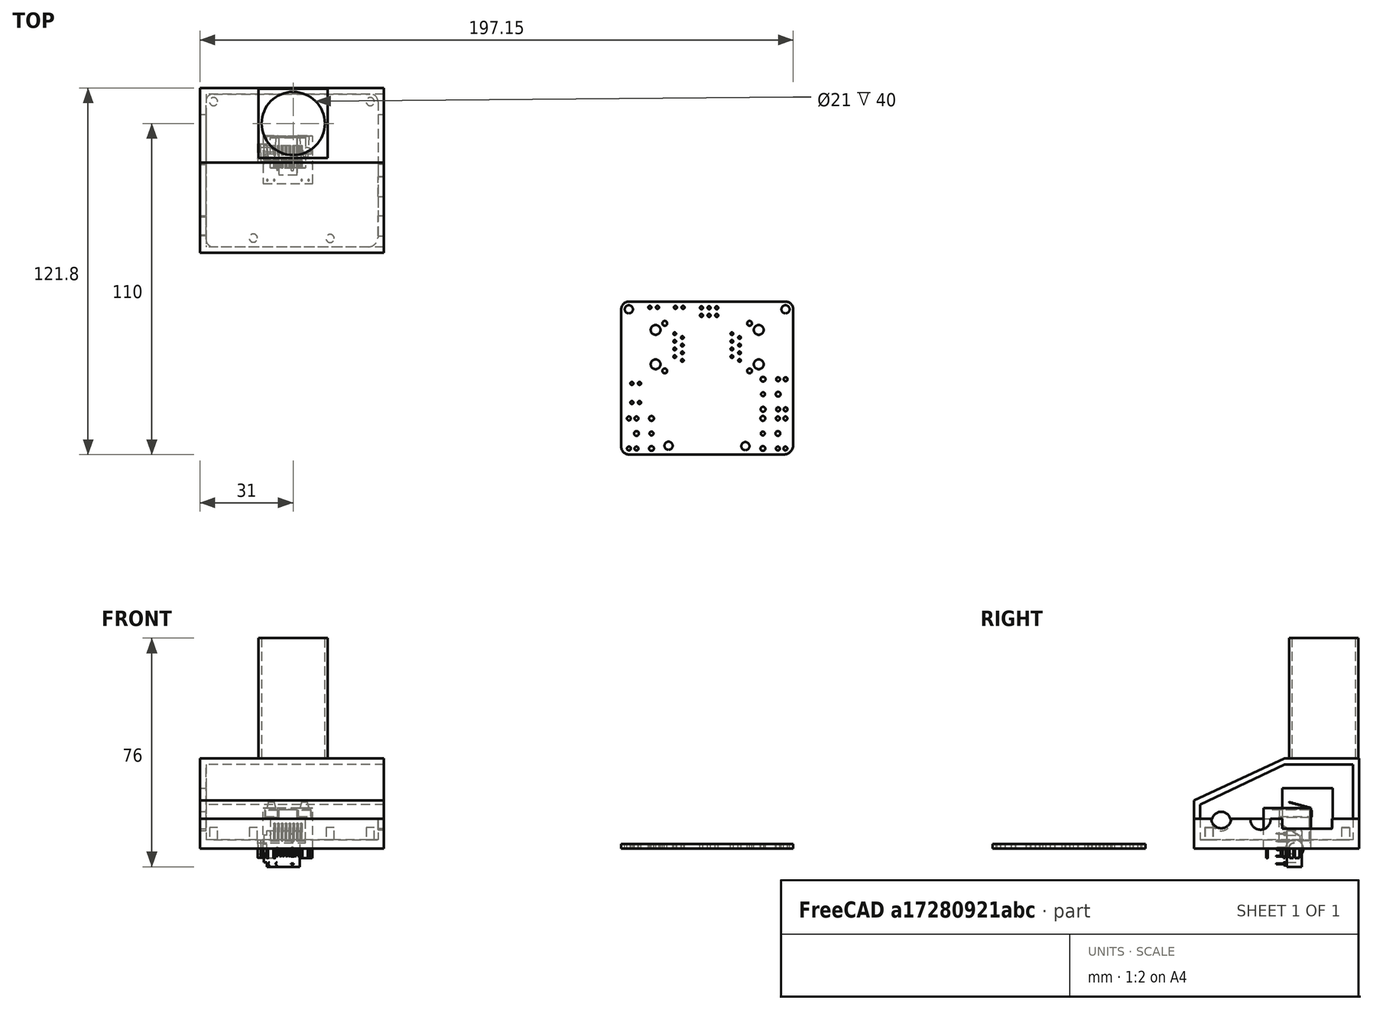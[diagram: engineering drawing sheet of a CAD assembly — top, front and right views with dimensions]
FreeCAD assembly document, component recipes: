
FREECAD ASSEMBLY — COMPONENT RECIPES ("FT81X-Mic")

This assembly document has 4 components, labeled P0..P3 below (a component is one placed body or linked part). 2 of them carry a construction recipe — the FreeCAD feature program that regenerates the part from scratch, quoted from this document or its linked companion documents; the rest are supplied as boundary geometry only. No exploded tour is included for this assembly.
COMPONENT P0 — recipe-attached ("Body", modeled in this document).
Construction recipe (the document's own serialized feature program — sketch geometry with constraints, then the solid features built on it; lengths are millimeters unless a unit is written):

FEATURE [PartDesign::SubShapeBinder] Binder
  BindMode = 0
  ClaimChildren = false
  Context = -> Body [Binder.]
  Fuse = false
  MakeFace = true
  PartialLoad = false
  Relative = true
  Support = -> [LinkGroup]
  _Version = 2
FEATURE [Sketcher::SketchObject] Sketch
  ExternalGeometry = -> [Binder]
  FullyConstrained = true
  MapMode = 5
  Support = -> [XY_Plane]
  sketch-geometry (4):
    g0: LineSegment StartX=-25.7 StartY=24.0101 StartZ=0 EndX=35.45 EndY=24.0101 EndZ=0
    g1: LineSegment StartX=35.45 StartY=24.0101 StartZ=0 EndX=35.45 EndY=-30.7899 EndZ=0
    g2: LineSegment StartX=35.45 StartY=-30.7899 StartZ=0 EndX=-25.7 EndY=-30.7899 EndZ=0
    g3: LineSegment StartX=-25.7 StartY=-30.7899 StartZ=0 EndX=-25.7 EndY=24.0101 EndZ=0
  constraints (12):
    c: Coincident(g0,g1)
    c: Coincident(g1,g2)
    c: Coincident(g2,g3)
    c: Coincident(g3,g0)
    c: Horizontal(g0)
    c: Horizontal(g2)
    c: Vertical(g1)
    c: Vertical(g3)
    c: DistanceY(g-3,g0) = 2
    c: DistanceY(g1,g-7) = 2
    c: DistanceX(g2,g-6) = 2
    c: DistanceX(g-8,g0) = 2
FEATURE [PartDesign::Pad] Pad
  Direction = (1,1,1)
  Length = 10
  Length2 = 100
  Profile = -> Sketch
  Type = 0
FEATURE [Sketcher::SketchObject] Sketch001
  ExternalGeometry = -> [Binder]
  FullyConstrained = true
  MapMode = 5
  Placement = pos=(0,0,10) rot=(0,0,1;0rad)
  Support = -> [Pad]
  sketch-geometry (8):
    g0: ArcOfCircle CenterX=30.91 CenterY=19.4701 CenterZ=0 NormalX=0 NormalY=0 NormalZ=1 AngleXU=0 Radius=2.53999 StartAngle=6.28318 EndAngle=7.85399
    g1: ArcOfCircle CenterX=30.275 CenterY=-25.6149 CenterZ=0 NormalX=0 NormalY=0 NormalZ=1 AngleXU=0 Radius=3.17501 StartAngle=4.71239 EndAngle=6.28318
    g2: ArcOfCircle CenterX=-21.16 CenterY=-26.25 CenterZ=0 NormalX=0 NormalY=0 NormalZ=1 AngleXU=0 Radius=2.53999 StartAngle=3.14159 EndAngle=4.71239
    g3: ArcOfCircle CenterX=-21.16 CenterY=19.4701 CenterZ=0 NormalX=0 NormalY=0 NormalZ=1 AngleXU=0 Radius=2.53997 StartAngle=1.57078 EndAngle=3.1416
    g4: LineSegment StartX=-21.16 StartY=22.0101 StartZ=0 EndX=30.91 EndY=22.0101 EndZ=0
    g5: LineSegment StartX=33.45 StartY=19.4701 StartZ=0 EndX=33.45 EndY=-25.6149 EndZ=0
    g6: LineSegment StartX=30.275 StartY=-28.7899 StartZ=0 EndX=-21.16 EndY=-28.7899 EndZ=0
    g7: LineSegment StartX=-23.7 StartY=-26.2499 StartZ=0 EndX=-23.7 EndY=19.4701 EndZ=0
  constraints (20):
    c: Coincident(g0,g-10)
    c: Coincident(g0,g-10)
    c: Coincident(g0,g-10)
    c: Coincident(g1,g-8)
    c: Coincident(g1,g-9)
    c: Coincident(g1,g-8)
    c: Coincident(g2,g-6)
    c: Coincident(g2,g-6)
    c: Coincident(g2,g-7)
    c: Coincident(g3,g-4)
    c: Coincident(g3,g-5)
    c: Coincident(g3,g-4)
    c: Coincident(g4,g3)
    c: Coincident(g4,g0)
    c: Coincident(g5,g0)
    c: Coincident(g5,g1)
    c: Coincident(g6,g1)
    c: Coincident(g6,g2)
    c: Coincident(g7,g2)
    c: Coincident(g7,g3)
FEATURE [PartDesign::Pocket] Pocket
  BaseFeature = -> Pad
  Length = 7
  Length2 = 100
  Profile = -> Sketch001
  Type = 0
FEATURE [Sketcher::SketchObject] Sketch002
  ExternalGeometry = -> [Binder,Pocket]
  FullyConstrained = true
  MapMode = 5
  Placement = pos=(-25.7,0,0) rot=(0.57735,-0.57735,-0.57735;2.0944rad)
  Support = -> [Pocket]
  sketch-geometry (5):
    g0: Circle CenterX=21.8049 CenterY=9.15 CenterZ=0 NormalX=0 NormalY=0 NormalZ=1 AngleXU=0 Radius=3.21
    g1: LineSegment StartX=-15.2571 StartY=6.65 StartZ=0 EndX=1.25294 EndY=6.65 EndZ=0
    g2: LineSegment StartX=1.25294 StartY=6.65 StartZ=0 EndX=1.25294 EndY=10 EndZ=0
    g3: LineSegment StartX=1.25294 StartY=10 StartZ=0 EndX=-15.2571 EndY=10 EndZ=0
    g4: LineSegment StartX=-15.2571 StartY=10 StartZ=0 EndX=-15.2571 EndY=6.65 EndZ=0
  constraints (13):
    c: Symmetric(g-10,g-10,g0)
    c: Diameter(g0) = 6.42
    c: Coincident(g1,g2)
    c: Coincident(g2,g3)
    c: Coincident(g3,g4)
    c: Coincident(g4,g1)
    c: Horizontal(g1)
    c: Horizontal(g3)
    c: Vertical(g2)
    c: Vertical(g4)
    c: Coincident(g1,g-7)
    c: DistanceX(g1,g-5) = 0
    c: PointOnObject(g3,g-11)
FEATURE [PartDesign::Pocket] Pocket001
  BaseFeature = -> Pocket
  Length = 5
  Length2 = 100
  Profile = -> Sketch002
  Type = 0
FEATURE [Sketcher::SketchObject] Sketch003
  ExternalGeometry = -> [Binder,Pocket001]
  FullyConstrained = true
  MapMode = 5
  Placement = pos=(35.45,0,0) rot=(0.57735,0.57735,0.57735;2.0944rad)
  Support = -> [Pocket001]
  sketch-geometry (6):
    g0: Circle CenterX=-21.8049 CenterY=10.15 CenterZ=0 NormalX=0 NormalY=0 NormalZ=1 AngleXU=0 Radius=3.34
    g1: Circle CenterX=-8.77094 CenterY=9.65 CenterZ=0 NormalX=0 NormalY=0 NormalZ=1 AngleXU=0 Radius=3.34
    g2: LineSegment StartX=-1.46294 StartY=6.65 StartZ=0 EndX=15.0471 EndY=6.65 EndZ=0
    g3: LineSegment StartX=15.0471 StartY=6.65 StartZ=0 EndX=15.0471 EndY=10 EndZ=0
    g4: LineSegment StartX=15.0471 StartY=10 StartZ=0 EndX=-1.46294 EndY=10 EndZ=0
    g5: LineSegment StartX=-1.46294 StartY=10 StartZ=0 EndX=-1.46294 EndY=6.65 EndZ=0
  constraints (15):
    c: Equal(g1,g0)
    c: Symmetric(g-6,g-6,g0)
    c: Symmetric(g-4,g-4,g1)
    c: Diameter(g0) = 6.68
    c: Coincident(g2,g3)
    c: Coincident(g3,g4)
    c: Coincident(g4,g5)
    c: Coincident(g5,g2)
    c: Horizontal(g2)
    c: Horizontal(g4)
    c: Vertical(g3)
    c: Vertical(g5)
    c: Coincident(g2,g-8)
    c: DistanceX(g2,g-9) = 0
    c: PointOnObject(g3,g-10)
FEATURE [PartDesign::Pocket] Pocket002
  BaseFeature = -> Pocket001
  Length = 5
  Length2 = 100
  Profile = -> Sketch003
  Type = 0
FEATURE [Sketcher::SketchObject] Sketch009
  ExternalGeometry = -> [Binder]
  FullyConstrained = false
  MapMode = 5
  Placement = pos=(0,0,3) rot=(0,0,1;0rad)
  Support = -> [Pocket002]
  sketch-geometry (5):
    g0: Circle CenterX=-7.95202 CenterY=-25.8689 CenterZ=0 NormalX=0 NormalY=0 NormalZ=1 AngleXU=0 Radius=1.37516
    g1: Circle CenterX=-7.95202 CenterY=-25.8689 CenterZ=0 NormalX=0 NormalY=0 NormalZ=1 AngleXU=0 Radius=1.35
    g2: Circle CenterX=17.575 CenterY=-25.9959 CenterZ=0 NormalX=0 NormalY=0 NormalZ=1 AngleXU=0 Radius=1.35
    g3: Circle CenterX=30.91 CenterY=19.4701 CenterZ=0 NormalX=0 NormalY=0 NormalZ=1 AngleXU=0 Radius=1.35
    g4: Circle CenterX=-21.16 CenterY=19.4701 CenterZ=0 NormalX=0 NormalY=0 NormalZ=1 AngleXU=0 Radius=1.35
  constraints (9):
    c: Coincident(g0,g-5)
    c: Coincident(g1,g0)
    c: Coincident(g2,g-6)
    c: Coincident(g3,g-4)
    c: Coincident(g4,g-3)
    c: Equal(g4,g1)
    c: Equal(g1,g-6)
    c: Equal(g-6,g2)
    c: Equal(g2,g3)
FEATURE [PartDesign::Pad] Pad003
  BaseFeature = -> Pocket002
  Direction = (1,1,1)
  Length = 4
  Length2 = 100
  Profile = -> Sketch009
  Type = 0
FEATURE [PartDesign::Body] Body
  Group = -> [Binder,Sketch,Pad,Sketch001,Pocket,Sketch002,Pocket001,Sketch003,Pocket002,Sketch009,Pad003]
  Origin = -> Origin
  Tip = -> Pad003
COMPONENT P1 — recipe-attached ("Body001", modeled in this document).
Construction recipe (the document's own serialized feature program — sketch geometry with constraints, then the solid features built on it; lengths are millimeters unless a unit is written):

FEATURE [PartDesign::SubShapeBinder] Binder001
  BindMode = 0
  ClaimChildren = false
  Context = -> Body001 [Binder001.]
  Fuse = false
  MakeFace = true
  PartialLoad = false
  Relative = true
  Support = -> [Body]
  _Version = 2
FEATURE [Sketcher::SketchObject] Sketch004
  ExternalGeometry = -> [Binder001]
  FullyConstrained = true
  MapMode = 5
  Support = -> [XY_Plane001]
  sketch-geometry (4):
    g0: LineSegment StartX=-25.7 StartY=24.0101 StartZ=0 EndX=35.45 EndY=24.0101 EndZ=0
    g1: LineSegment StartX=35.45 StartY=24.0101 StartZ=0 EndX=35.45 EndY=-30.7899 EndZ=0
    g2: LineSegment StartX=35.45 StartY=-30.7899 StartZ=0 EndX=-25.7 EndY=-30.7899 EndZ=0
    g3: LineSegment StartX=-25.7 StartY=-30.7899 StartZ=0 EndX=-25.7 EndY=24.0101 EndZ=0
  constraints (10):
    c: Coincident(g0,g1)
    c: Coincident(g1,g2)
    c: Coincident(g2,g3)
    c: Coincident(g3,g0)
    c: Horizontal(g0)
    c: Horizontal(g2)
    c: Vertical(g1)
    c: Vertical(g3)
    c: Coincident(g0,g-4)
    c: Coincident(g1,g-5)
FEATURE [PartDesign::Pad] Pad001
  Direction = (1,1,1)
  Length = 20
  Length2 = 100
  Profile = -> Sketch004
  Type = 0
FEATURE [PartDesign::SubShapeBinder] Binder002
  BindMode = 0
  ClaimChildren = false
  Context = -> Body001 [Binder002.]
  Fuse = false
  MakeFace = true
  PartialLoad = false
  Relative = true
  Support = -> [LinkGroup]
  _Version = 2
FEATURE [Sketcher::SketchObject] Sketch005
  ExternalGeometry = -> [Binder002,Pad001]
  FullyConstrained = true
  MapMode = 5
  Placement = pos=(35.45,0,0) rot=(0.57735,0.57735,0.57735;2.0944rad)
  Support = -> [Pad001]
  sketch-geometry (3):
    g0: LineSegment StartX=-30.7899 StartY=20 StartZ=0 EndX=-0.789942 EndY=20 EndZ=0
    g1: LineSegment StartX=-30.7899 StartY=6 StartZ=0 EndX=-0.789942 EndY=20 EndZ=0
    g2: LineSegment StartX=-30.7899 StartY=20 StartZ=0 EndX=-30.7899 EndY=6 EndZ=0
  constraints (8):
    c: PointOnObject(g0,g-15)
    c: Distance(g0) = 30
    c: Coincident(g1,g0)
    c: Coincident(g0,g-15)
    c: Coincident(g2,g0)
    c: PointOnObject(g2,g-13)
    c: Distance(g2) = 14
    c: Coincident(g2,g1)
FEATURE [PartDesign::Pocket] Pocket003
  BaseFeature = -> Pad001
  Length = 0
  Length2 = 100
  Profile = -> Sketch005
  Type = 1
FEATURE [Sketcher::SketchObject] Sketch006
  ExternalGeometry = -> [Binder002,Pocket003]
  FullyConstrained = true
  MapMode = 5
  Placement = pos=(35.45,0,0) rot=(0.57735,0.57735,0.57735;2.0944rad)
  Support = -> [Pocket003]
  sketch-geometry (6):
    g0: LineSegment StartX=-1.46294 StartY=10.11 StartZ=0 EndX=15.0471 EndY=10.11 EndZ=0
    g1: LineSegment StartX=15.0471 StartY=10.11 StartZ=0 EndX=15.0471 EndY=-0.889997 EndZ=0
    g2: LineSegment StartX=15.0471 StartY=-0.889997 StartZ=0 EndX=-1.46294 EndY=-0.889997 EndZ=0
    g3: LineSegment StartX=-1.46294 StartY=-0.889997 StartZ=0 EndX=-1.46294 EndY=10.11 EndZ=0
    g4: Circle CenterX=-8.77094 CenterY=-0.349997 CenterZ=0 NormalX=0 NormalY=0 NormalZ=1 AngleXU=0 Radius=3.34
    g5: Circle CenterX=-21.8049 CenterY=0.150003 CenterZ=0 NormalX=0 NormalY=0 NormalZ=1 AngleXU=0 Radius=3.34
  constraints (15):
    c: Coincident(g0,g1)
    c: Coincident(g1,g2)
    c: Coincident(g2,g3)
    c: Coincident(g3,g0)
    c: Horizontal(g0)
    c: Horizontal(g2)
    c: Vertical(g1)
    c: Vertical(g3)
    c: Coincident(g0,g-7)
    c: DistanceX(g0,g-9) = 0
    c: Distance(g3) = 11
    c: Equal(g4,g5)
    c: Diameter(g5) = 6.68
    c: Symmetric(g-4,g-4,g5)
    c: Symmetric(g-6,g-6,g4)
FEATURE [PartDesign::Pocket] Pocket004
  BaseFeature = -> Pocket003
  Length = 5
  Length2 = 100
  Profile = -> Sketch006
  Type = 0
FEATURE [Sketcher::SketchObject] Sketch007
  ExternalGeometry = -> [Pocket004,Binder002]
  FullyConstrained = true
  MapMode = 5
  Placement = pos=(-25.7,0,0) rot=(0.57735,-0.57735,-0.57735;2.0944rad)
  Support = -> [Pocket004]
  sketch-geometry (5):
    g0: LineSegment StartX=-15.2571 StartY=10.11 StartZ=0 EndX=0 EndY=10.11 EndZ=0
    g1: LineSegment StartX=0 StartY=10.11 StartZ=0 EndX=0 EndY=0 EndZ=0
    g2: LineSegment StartX=0 StartY=0 StartZ=0 EndX=-15.2571 EndY=0 EndZ=0
    g3: LineSegment StartX=-15.2571 StartY=0 StartZ=0 EndX=-15.2571 EndY=10.11 EndZ=0
    g4: Circle CenterX=21.8049 CenterY=-0.849997 CenterZ=0 NormalX=0 NormalY=0 NormalZ=1 AngleXU=0 Radius=3.34
  constraints (12):
    c: Coincident(g0,g1)
    c: Coincident(g1,g2)
    c: Coincident(g2,g3)
    c: Coincident(g3,g0)
    c: Horizontal(g0)
    c: Horizontal(g2)
    c: Vertical(g1)
    c: Vertical(g3)
    c: Coincident(g0,g-7)
    c: Coincident(g1,g-1)
    c: Diameter(g4) = 6.68
    c: Symmetric(g-6,g-6,g4)
FEATURE [PartDesign::Pocket] Pocket005
  BaseFeature = -> Pocket004
  Length = 17
  Length2 = 100
  Profile = -> Sketch007
  Type = 0
FEATURE [Sketcher::SketchObject] Sketch008
  ExternalGeometry = -> [Pocket005]
  FullyConstrained = true
  MapMode = 5
  Placement = pos=(0,0,20) rot=(0,0,1;0rad)
  Support = -> [Pocket005]
  sketch-geometry (5):
    g0: Circle CenterX=5.29998 CenterY=12.2101 CenterZ=0 NormalX=0 NormalY=0 NormalZ=1 AngleXU=0 Radius=10.5
    g1: LineSegment StartX=-6.20002 StartY=23.7101 StartZ=0 EndX=16.8 EndY=23.7101 EndZ=0
    g2: LineSegment StartX=16.8 StartY=23.7101 StartZ=0 EndX=16.8 EndY=0.710058 EndZ=0
    g3: LineSegment StartX=16.8 StartY=0.710058 StartZ=0 EndX=-6.20002 EndY=0.710058 EndZ=0
    g4: LineSegment StartX=-6.20002 StartY=0.710058 StartZ=0 EndX=-6.20002 EndY=23.7101 EndZ=0
  constraints (14):
    c: DistanceY(g-6,g0) = 13
    c: DistanceX(g-6,g0) = 31
    c: Coincident(g1,g2)
    c: Coincident(g2,g3)
    c: Coincident(g3,g4)
    c: Coincident(g4,g1)
    c: Horizontal(g1)
    c: Horizontal(g3)
    c: Vertical(g2)
    c: Vertical(g4)
    c: Symmetric(g3,g1,g0)
    c: Distance(g2) = 23
    c: Distance(g1) = 23
    c: Diameter(g0) = 21
FEATURE [PartDesign::Pad] Pad002
  BaseFeature = -> Pocket005
  Direction = (1,1,1)
  Length = 40
  Length2 = 100
  Profile = -> Sketch008
  Type = 0
FEATURE [Sketcher::SketchObject] Sketch010
  ExternalGeometry = -> [Pocket005]
  FullyConstrained = true
  MapMode = 5
  Placement = pos=(35.45,0,0) rot=(0.57735,0.57735,0.57735;2.0944rad)
  Support = -> [Pocket005]
  sketch-geometry (5):
    g0: LineSegment StartX=-28.7899 StartY=0 StartZ=0 EndX=-28.7899 EndY=4.6 EndZ=0
    g1: LineSegment StartX=-28.7899 StartY=4.6 StartZ=0 EndX=-0.789942 EndY=18 EndZ=0
    g2: LineSegment StartX=-0.789942 StartY=18 StartZ=0 EndX=22.0101 EndY=18 EndZ=0
    g3: LineSegment StartX=22.0101 StartY=18 StartZ=0 EndX=22.0101 EndY=0 EndZ=0
    g4: LineSegment StartX=-28.7899 StartY=0 StartZ=0 EndX=22.0101 EndY=0 EndZ=0
  constraints (15):
    c: DistanceY(g2,g-6) = 2
    c: Coincident(g1,g2)
    c: Parallel(g0,g-4)
    c: Coincident(g0,g1)
    c: DistanceX(g-4,g0) = 2
    c: DistanceY(g1,g-5) = 2
    c: DistanceX(g-5,g1) = 0
    c: DistanceY(g0,g-4) = 1.4
    c: Coincident(g3,g2)
    c: PointOnObject(g3,g-1)
    c: Vertical(g3)
    c: DistanceX(g3,g-6) = 2
    c: PointOnObject(g0,g-1)
    c: Coincident(g4,g0)
    c: Coincident(g4,g3)
FEATURE [PartDesign::Pocket] Pocket006
  BaseFeature = -> Pad002
  Length = 5
  Length2 = 100
  Profile = -> Sketch010
  Type = 1
FEATURE [Sketcher::SketchObject] Sketch011
  ExternalGeometry = -> [Pocket006,Binder002]
  FullyConstrained = true
  MapMode = 5
  Placement = pos=(-25.7,0,0) rot=(0.57735,-0.57735,-0.57735;2.0944rad)
  Support = -> [Pocket006]
  sketch-geometry (11):
    g0: LineSegment StartX=-22.0101 StartY=0 StartZ=0 EndX=-22.0101 EndY=18 EndZ=0
    g1: LineSegment StartX=-22.0101 StartY=18 StartZ=0 EndX=0.789942 EndY=18 EndZ=0
    g2: LineSegment StartX=0.789942 StartY=18 StartZ=0 EndX=28.7899 EndY=4.6 EndZ=0
    g3: LineSegment StartX=28.7899 StartY=4.6 StartZ=0 EndX=28.7899 EndY=0 EndZ=0
    g4: LineSegment StartX=-22.0101 StartY=0 StartZ=0 EndX=-15.2571 EndY=0 EndZ=0
    g5: LineSegment StartX=-15.2571 StartY=0 StartZ=0 EndX=-15.2571 EndY=10.11 EndZ=0
    g6: LineSegment StartX=-15.2571 StartY=10.11 StartZ=0 EndX=1.46294 EndY=10.11 EndZ=0
    g7: LineSegment StartX=1.46294 StartY=10.11 StartZ=0 EndX=1.46294 EndY=0 EndZ=0
    g8: LineSegment StartX=1.46294 StartY=0 StartZ=0 EndX=18.8049 EndY=0 EndZ=0
    g9: ArcOfCircle CenterX=21.8049 CenterY=-0.849997 CenterZ=0 NormalX=0 NormalY=0 NormalZ=1 AngleXU=0 Radius=3.11809 StartAngle=0.276096 EndAngle=2.8655
    g10: LineSegment StartX=24.8049 StartY=1e-16 StartZ=0 EndX=28.7899 EndY=0 EndZ=0
  constraints (26):
    c: Coincident(g0,g-4)
    c: Coincident(g0,g-4)
    c: Coincident(g1,g0)
    c: Coincident(g1,g-5)
    c: Coincident(g2,g1)
    c: Coincident(g2,g-6)
    c: Coincident(g3,g2)
    c: Coincident(g3,g-6)
    c: Coincident(g4,g0)
    c: Horizontal(g4)
    c: DistanceX(g4,g-7) = 0
    c: Coincident(g5,g4)
    c: Coincident(g5,g-7)
    c: Coincident(g6,g5)
    c: Coincident(g6,g-9)
    c: Coincident(g7,g6)
    c: Vertical(g7)
    c: DistanceY(g-1,g7) = 0
    c: Coincident(g8,g7)
    c: Horizontal(g8)
    c: DistanceX(g-10,g8) = 0
    c: Coincident(g9,g8)
    c: PointOnObject(g9,g-1)
    c: Symmetric(g-10,g-10,g9)
    c: Coincident(g10,g9)
    c: Coincident(g10,g3)
FEATURE [PartDesign::Pad] Pad004
  BaseFeature = -> Pocket006
  Direction = (1,1,1)
  Length = 2
  Length2 = 100
  Profile = -> Sketch011
  Reversed = true
  Type = 0
FEATURE [PartDesign::Body] Body001
  Group = -> [Sketch004,Binder001,Pad001,Binder002,Sketch005,Pocket003,Sketch006,Pocket004,Sketch007,Pocket005,Sketch008,Pad002,Sketch010,Pocket006,Sketch011,Pad004]
  Origin = -> Origin001
  Placement = pos=(0,0,10) rot=(0,0,1;0rad)
  Tip = -> Pad004
COMPONENT P2 — geometry summary ("RJ45_Amphenol_RJHSE538X001"; no construction recipe available for this part):
  bounding box: 56.6 x 18.7 x 16.7 mm
  tessellated surface: 31,108 triangles
  volume: 4892 mm^3 (28% of its bounding box)
  symmetry: 2-fold rotationally symmetric about the z axis
COMPONENT P3 — geometry summary ("FC68132"; no construction recipe available for this part):
  bounding box: 60.1 x 25.0 x 10.0 mm
  tessellated surface: 18,876 triangles
  volume: 2223 mm^3 (15% of its bounding box)
PROVENANCE & LICENSES
A FreeCAD (.FCStd) document from a public repository crawl; recipes are the document's own serialized feature recipes (and, for linked parts, companion documents' recipes).
License: as declared in the source repository (recorded in the dataset sidecar).
